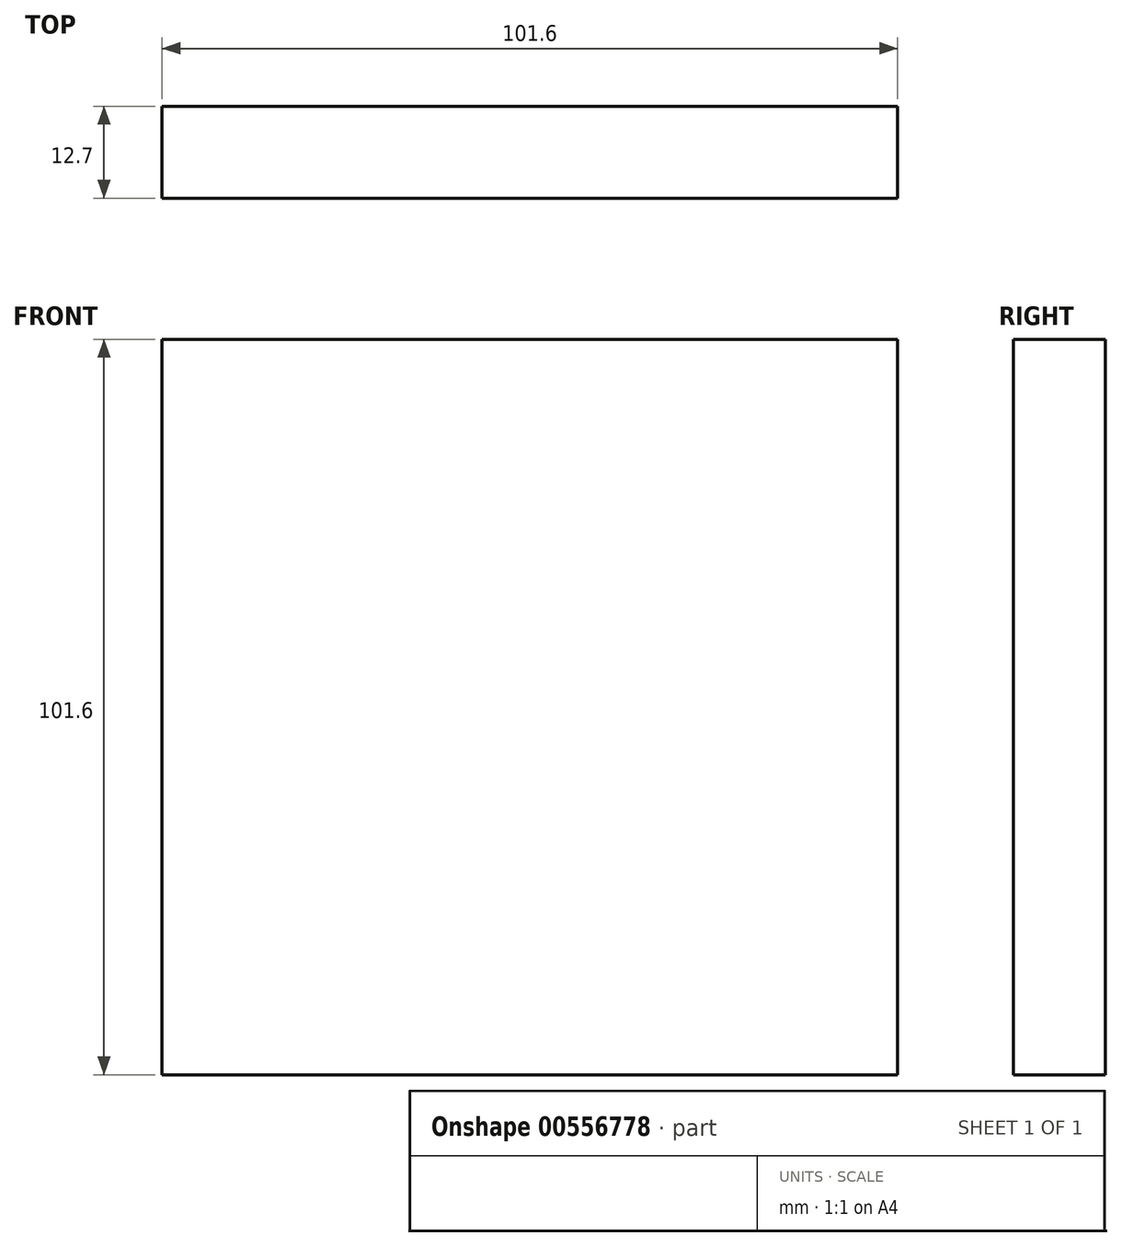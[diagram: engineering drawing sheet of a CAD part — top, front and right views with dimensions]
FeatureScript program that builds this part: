
annotation { "Feature Type Name" : "Feature", "Feature Type Description" : "" }
export const myFeature = defineFeature(function(context is Context, id is Id, definition is map)
    precondition{}
    {
        {
            var Q0;
            Q0=qCreatedBy(makeId("Front.planeOp"),FACE);
            var sketch = newSketch(context, id + "F0", { "sketchPlane" : qUnion([Q0])});
            skLineSegment(sketch, "E0.bottom", {"start": v(0, 0) * mm, "end": v(101.6, 0) * mm});
            skLineSegment(sketch, "E0.top", {"start": v(0, 101.6) * mm, "end": v(101.6, 101.6) * mm});
            skLineSegment(sketch, "E0.left", {"start": v(0, 0) * mm, "end": v(0, 101.6) * mm});
            skLineSegment(sketch, "E0.right", {"start": v(101.6, 0) * mm, "end": v(101.6, 101.6) * mm});
            skSolve(sketch);
        }
        {
            var Q0;
            Q0 = qSketchRegion(id + "F0", true);
            extrude(context, id + "F1", {"entities" : qUnion([Q0]), "oppositeDirection" : true, "depth" : 12.7 * mm, "offsetDistance" : 25.4 * mm});
        }
    });
